# Revit family: Towel_Bar-DXV-Percy-D35105240_Series
name_source: partatom
category: Specialty Equipment
revit_build: Autodesk Revit 2014 (Build: 20130308_1515(x64)
units: mm (PartAtom-declared; Revit-internal decimal feet)

## types (6) — shared parameters
Assembly Code = C1030200
Default Elevation = 40"
Height = 2 1/4"
Installation Type = Surface Mounted
Length = 3 7/16"
Manufacturer = DXV
Price = Prices may vary. Please consult Manufacturer Representative for most up-to-date price list.
URL = http://www.dxv.com
Warranty Documentation Link = https://www.dxv.com

## per-type parameters (varying)
| type | Description | Finish | Material | Product Documentation Link | Product Page URL | Width |
| D35105240.100 | Percy 24" Towl Bar | Brass-DXV-100-Polished Chrome | Brass-DXV-100-Polished Chrome | http://dxv01.blob.core.windows.net | http://www.dxv.com | 24" |
| D35105240.144 | Percy 24" Towl Bar | Brass-DXV-144-Brushed Nickel | Brass-DXV-144-Brushed Nickel | http://dxv01.blob.core.windows.net | http://www.dxv.com | 24" |
| D35105180.100 | Percy 18" Towl Bar | Brass-DXV-100-Polished Chrome | Brass-DXV-100-Polished Chrome | https://dxv01.blob.core.windows.net | https://www.dxv.com | 18" |
| D35105180.144 | Percy 18" Towl Bar | Brass-DXV-144-Brushed Nickel | Brass-DXV-144-Brushed Nickel | https://dxv01.blob.core.windows.net | https://www.dxv.com | 18" |
| D35105120.100 | Percy 12" Towl Bar | Brass-DXV-100-Polished Chrome | Brass-DXV-100-Polished Chrome | https://dxv01.blob.core.windows.net | https://www.dxv.com | 12" |
| D35105120.144 | Percy 12" Towl Bar | Brass-DXV-144-Brushed Nickel | Brass-DXV-144-Brushed Nickel | https://dxv01.blob.core.windows.net | https://www.dxv.com | 12" |

note: column(s) folded — value = type name in every type: Model

## geometry (parser evidence)
native form markers: Sweep x3
no freeform markers — native parametric forms only
